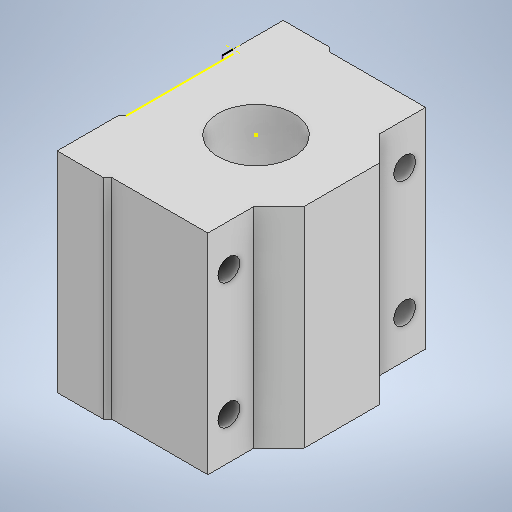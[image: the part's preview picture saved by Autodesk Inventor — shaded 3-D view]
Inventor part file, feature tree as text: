
AUTODESK INVENTOR PART (.ipt)
format: ipt  version: 2025 (Build 290162000, 162)  size: 280,064 bytes
history: native  units: in
note: dims shown in document units (in); Inventor stores cm internally (conversion verified against a paired STEP export)
features: sketch x6, extrude x2, mirror x2, hole x1
ambient origin geometry x8: Origin, YZ Plane, XZ Plane, XY Plane, X Axis, Y Axis, Z Axis, Center Point
bodies: Solid1 (feature_tree)
feature tree (11):
  extrude  "Extrusion1"  Depth=1.6142in
  sketch  "Sketch2"  dims[d2=2.126in d4=45.0deg]
  sketch  "Sketch3"  dims[d8=1.9685in d9=0.0in d12=135.0deg]
  extrude  "Extrusion2"  TaperAngle=45.0deg  [1 undecoded]
  sketch  "Sketch5"  dims[d17=0.2362in]
  sketch  "Sketch6"  dims[d20=0.2047in d21=0.2362in d22=0.2362in d23=0.4724in d24=90.0deg d25=0.315in d26=0.8108in]
  mirror  "Mirror1"
  mirror  "Mirror2"
  hole  "Hole1"  [1 undecoded]
  sketch  "Sketch1"  dims[d0=0.7087in d1=1.6142in]
  sketch  "Sketch4"  dims[d13=1.9685in d14=0.0in]
note: 2 required parameter values undecoded (feature->parameter linkage not recoverable at this tier; creation-order binding heuristic only, values carry confidence <= 0.55)
